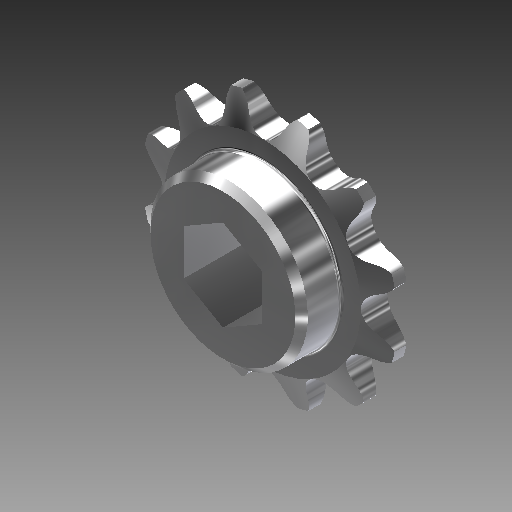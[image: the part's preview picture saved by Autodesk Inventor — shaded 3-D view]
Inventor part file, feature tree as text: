
AUTODESK INVENTOR PART (.ipt)
format: ipt  version: 2017 (Build 210142000, 142)  size: 511,488 bytes
history: native  units: in
note: dims shown in document units (in); Inventor stores cm internally (conversion verified against a paired STEP export)
features: chamfer x1, other x1, imported_body x1
ambient origin geometry x8: Origin, YZ Plane, XZ Plane, XY Plane, X Axis, Y Axis, Z Axis, Center Point
bodies: Body1 (feature_tree)
feature tree (3):
  chamfer  "Chamfer1"  [1 undecoded]
  other  "Sprocket 35_12T1"
  imported_body  "Base1"
note: 1 required parameter value undecoded (feature->parameter linkage not recoverable at this tier; creation-order binding heuristic only, values carry confidence <= 0.55)
